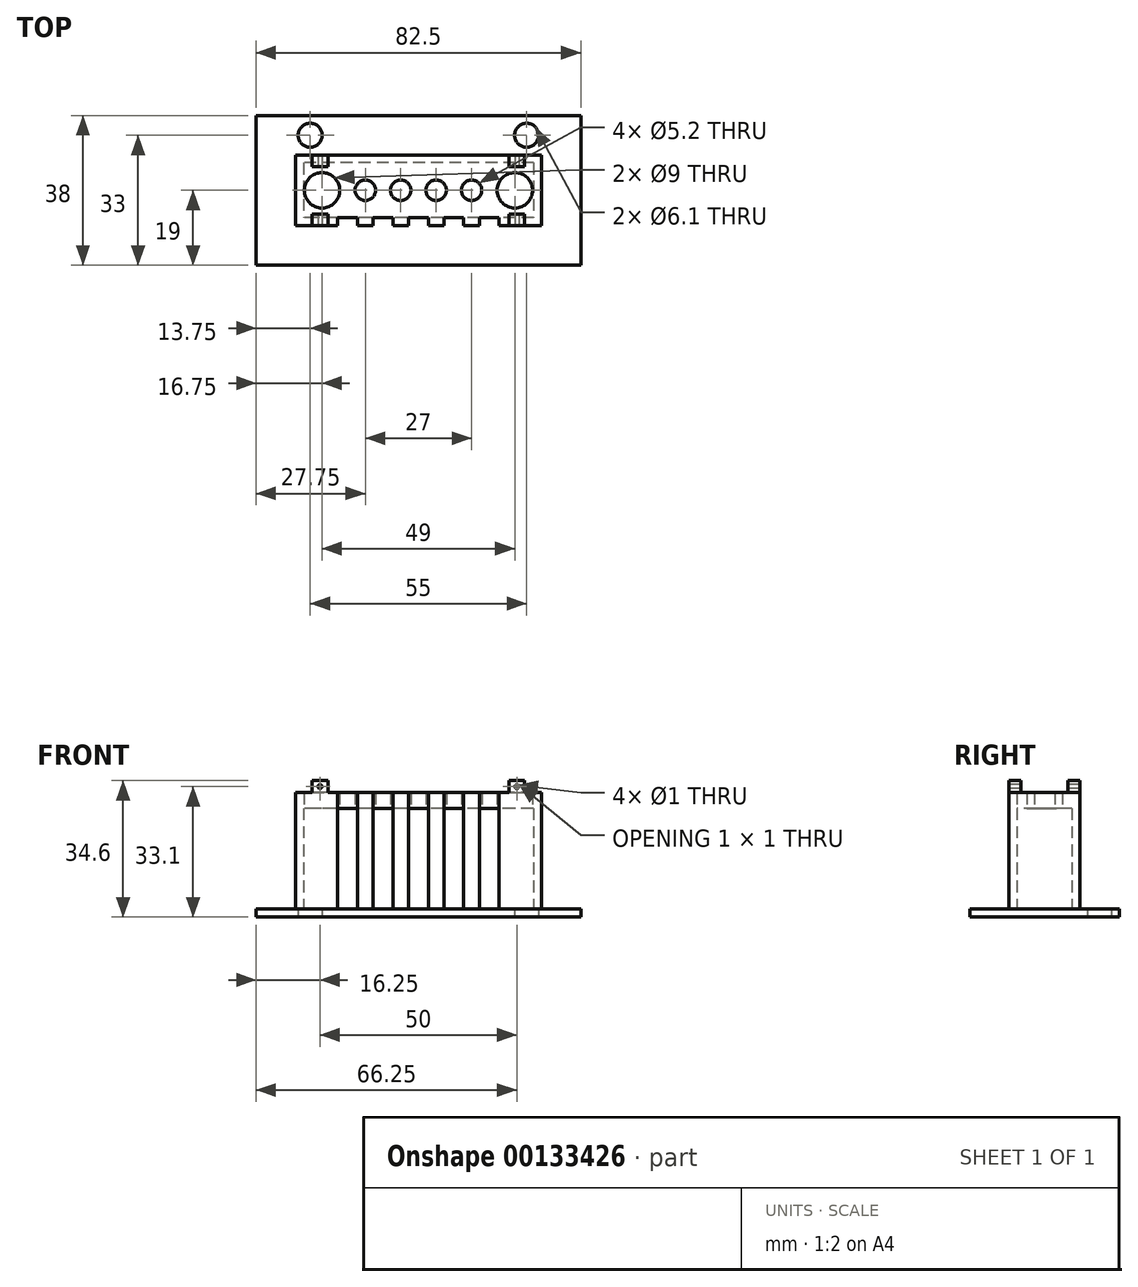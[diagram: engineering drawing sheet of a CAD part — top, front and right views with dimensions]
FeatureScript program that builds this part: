
annotation { "Feature Type Name" : "Feature", "Feature Type Description" : "" }
export const myFeature = defineFeature(function(context is Context, id is Id, definition is map)
    precondition{}
    {
        {
            var Q0;
            Q0=qCreatedBy(makeId("Top.planeOp"),FACE);
            var sketch = newSketch(context, id + "F0", { "sketchPlane" : qUnion([Q0])});
            skLineSegment(sketch, "E0.bottom", {"start": v(31.25, 9) * mm, "end": v(-31.25, 9) * mm});
            skLineSegment(sketch, "E0.top", {"start": v(31.25, -9) * mm, "end": v(-31.25, -9) * mm});
            skLineSegment(sketch, "E0.left", {"start": v(31.25, 9) * mm, "end": v(31.25, -9) * mm});
            skLineSegment(sketch, "E0.right", {"start": v(-31.25, 9) * mm, "end": v(-31.25, -9) * mm});
            skPoint(sketch, "E0.middle", {"position": v(0, 0) * mm});
            skLineSegment(sketch, "E1", {"start": v(-31.25, -9) * mm, "end": v(-31.25, 0) * mm});
            skLineSegment(sketch, "E2", {"start": v(-31.25, 0) * mm, "end": v(31.25, 0) * mm});
            skLineSegment(sketch, "E3", {"start": v(-13.5, 0) * mm, "end": v(-4.5, 0) * mm, "construction": true});
            skCircle(sketch, "E4", {"center": v(-4.5, 0) * mm, "radius": 2.6 * mm});
            skCircle(sketch, "E5.MirrorC", {"center": v(4.5, 0) * mm, "radius": 2.6 * mm});
            skLineSegment(sketch, "E6.0", {"start": v(29.25, -7) * mm, "end": v(-29.25, -7) * mm});
            skLineSegment(sketch, "E6.1", {"start": v(29.25, 7) * mm, "end": v(29.25, -7) * mm});
            skLineSegment(sketch, "E6.2", {"start": v(29.25, 7) * mm, "end": v(-29.25, 7) * mm});
            skLineSegment(sketch, "E6.3", {"start": v(-29.25, 7) * mm, "end": v(-29.25, -7) * mm});
            skCircle(sketch, "E7", {"center": v(-13.5, 0) * mm, "radius": 2.6 * mm});
            skLineSegment(sketch, "E8", {"start": v(4.5, 0) * mm, "end": v(4.5, 0) * mm});
            skCircle(sketch, "E9.MirrorC", {"center": v(13.5, 0) * mm, "radius": 2.6 * mm});
            skLineSegment(sketch, "E10.0", {"start": v(41.25, 19) * mm, "end": v(-41.25, 19) * mm});
            skLineSegment(sketch, "E10.1", {"start": v(41.25, 19) * mm, "end": v(41.25, -19) * mm});
            skLineSegment(sketch, "E10.2", {"start": v(41.25, -19) * mm, "end": v(-41.25, -19) * mm});
            skLineSegment(sketch, "E10.3", {"start": v(-41.25, 19) * mm, "end": v(-41.25, -19) * mm});
            skLineSegment(sketch, "E11", {"start": v(-41.25, 19) * mm, "end": v(-41.25, 14) * mm});
            skLineSegment(sketch, "E12", {"start": v(-41.25, 14) * mm, "end": v(-36.25, 14) * mm});
            skLineSegment(sketch, "E13", {"start": v(-13.5, 0) * mm, "end": v(-36.25, 0) * mm});
            skLineSegment(sketch, "E14", {"start": v(-36.25, 0) * mm, "end": v(-36.25, 14) * mm});
            skCircle(sketch, "E15.MirrorC", {"center": v(27.5, 14) * mm, "radius": 3.05 * mm});
            skCircle(sketch, "E16.MirrorC", {"center": v(-27.5, 14) * mm, "radius": 3.05 * mm});
            skLineSegment(sketch, "E17", {"start": v(0, 0) * mm, "end": v(24.5, 0) * mm});
            skCircle(sketch, "E18", {"center": v(24.5, 0) * mm, "radius": 4.5 * mm});
            skCircle(sketch, "E19.MirrorC", {"center": v(-24.5, 0) * mm, "radius": 4.5 * mm});
            skSolve(sketch);
        }
        {
            var Q0;
            {var subQ8=sQuery(id+"F0.wireOp",EDGE,"E0.top");Q0=makeQuery(id+"F0.imprint","IMPRINT",FACE,{"disambiguationData":[TD([[makeQuery(id+"F0.imprint","IMPRINT",EDGE,{"derivedFrom":subQ8}),-1.0]])]});}
            var Q1;
            {var subQ6=sQuery(id+"F0.wireOp",EDGE,"E0.bottom");Q1=makeQuery(id+"F0.imprint","IMPRINT",FACE,{"disambiguationData":[TD([[makeQuery(id+"F0.imprint","IMPRINT",EDGE,{"derivedFrom":subQ6}),1.0]])]});}
            extrude(context, id + "F1", {"entities" : qUnion([Q0, Q1]), "depth" : 31.6 * mm});
        }
        {
            var Q0;
            {var subQ8=sQuery(id+"F0.wireOp",EDGE,"E6.2");Q0=makeQuery(id+"F0.imprint","IMPRINT",FACE,{"disambiguationData":[TD([[makeQuery(id+"F0.imprint","IMPRINT",EDGE,{"derivedFrom":subQ8}),1.0]])]});}
            var Q1;
            {var subQ0=sQuery(id+"F0.wireOp",EDGE,"E6.0");Q1=makeQuery(id+"F0.imprint","IMPRINT",FACE,{"disambiguationData":[TD([[makeQuery(id+"F0.imprint","IMPRINT",EDGE,{"derivedFrom":subQ0}),-1.0]])]});}
            extrude(context, id + "F2", {"entities" : qUnion([Q0, Q1]), "operationType" : NewBodyOperationType.ADD, "depth" : 31.6 * mm, "hasSecondDirection" : true, "secondDirectionOppositeDirection" : false, "secondDirectionDepth" : 27.6 * mm});
        }
        {
            var Q0;
            {var subQ0=sQuery(id+"F0.wireOp",EDGE,"E0.bottom");Q0=makeQuery(id+"F0.imprint","IMPRINT",FACE,{"disambiguationData":[TD([[makeQuery(id+"F0.imprint","IMPRINT",EDGE,{"derivedFrom":subQ0}),-1.0]])]});}
            extrude(context, id + "F3", {"entities" : qUnion([Q0]), "operationType" : NewBodyOperationType.ADD, "depth" : 2 * mm});
        }
        {
            var Q0;
            Q0=makeQuery(id+"F1.opExtrude","SWEPT_FACE",FACE,{"disambiguationData":[OSD([sQuery(id+"F0.wireOp",EDGE,"E0.top")])]});
            var sketch = newSketch(context, id + "F4", { "sketchPlane" : qUnion([Q0])});
            skLineSegment(sketch, "E20", {"start": v(0, 2) * mm, "end": v(0, 31.6) * mm});
            skLineSegment(sketch, "E21.bottom", {"start": v(2.5, 31.6) * mm, "end": v(-2.5, 31.6) * mm});
            skLineSegment(sketch, "E21.top", {"start": v(2.5, 2) * mm, "end": v(-2.5, 2) * mm});
            skLineSegment(sketch, "E21.left", {"start": v(2.5, 31.6) * mm, "end": v(2.5, 2) * mm});
            skLineSegment(sketch, "E21.right", {"start": v(-2.5, 31.6) * mm, "end": v(-2.5, 2) * mm});
            skPoint(sketch, "E21.middle", {"position": v(0, 16.8) * mm});
            skLineSegment(sketch, "E22", {"start": v(0, 2) * mm, "end": v(-9, 2) * mm});
            skLineSegment(sketch, "E23", {"start": v(0, 2) * mm, "end": v(9, 2) * mm});
            skLineSegment(sketch, "E24", {"start": v(9, 2) * mm, "end": v(18, 2) * mm});
            skLineSegment(sketch, "E25", {"start": v(-9, 2) * mm, "end": v(-18, 2) * mm});
            skLineSegment(sketch, "E26", {"start": v(-18, 2) * mm, "end": v(-18, 31.6) * mm});
            skLineSegment(sketch, "E27", {"start": v(-9, 2) * mm, "end": v(-9, 31.6) * mm});
            skLineSegment(sketch, "E28", {"start": v(9, 2) * mm, "end": v(9, 31.6) * mm});
            skLineSegment(sketch, "E29", {"start": v(18, 2) * mm, "end": v(18, 31.6) * mm});
            skLineSegment(sketch, "E30.bottom", {"start": v(-15.5, 31.6) * mm, "end": v(-20.5, 31.6) * mm});
            skLineSegment(sketch, "E30.top", {"start": v(-15.5, 2) * mm, "end": v(-20.5, 2) * mm});
            skLineSegment(sketch, "E30.left", {"start": v(-15.5, 31.6) * mm, "end": v(-15.5, 2) * mm});
            skLineSegment(sketch, "E30.right", {"start": v(-20.5, 31.6) * mm, "end": v(-20.5, 2) * mm});
            skPoint(sketch, "E30.middle", {"position": v(-18, 16.8) * mm});
            skLineSegment(sketch, "E31.bottom", {"start": v(-6.5, 31.6) * mm, "end": v(-11.5, 31.6) * mm});
            skLineSegment(sketch, "E31.top", {"start": v(-6.5, 2) * mm, "end": v(-11.5, 2) * mm});
            skLineSegment(sketch, "E31.left", {"start": v(-6.5, 31.6) * mm, "end": v(-6.5, 2) * mm});
            skLineSegment(sketch, "E31.right", {"start": v(-11.5, 31.6) * mm, "end": v(-11.5, 2) * mm});
            skPoint(sketch, "E31.middle", {"position": v(-9, 16.8) * mm});
            skLineSegment(sketch, "E32.bottom", {"start": v(11.5, 31.6) * mm, "end": v(6.5, 31.6) * mm});
            skLineSegment(sketch, "E32.top", {"start": v(11.5, 2) * mm, "end": v(6.5, 2) * mm});
            skLineSegment(sketch, "E32.left", {"start": v(11.5, 31.6) * mm, "end": v(11.5, 2) * mm});
            skLineSegment(sketch, "E32.right", {"start": v(6.5, 31.6) * mm, "end": v(6.5, 2) * mm});
            skPoint(sketch, "E32.middle", {"position": v(9, 16.8) * mm});
            skLineSegment(sketch, "E33.bottom", {"start": v(20.5, 31.6) * mm, "end": v(15.5, 31.6) * mm});
            skLineSegment(sketch, "E33.top", {"start": v(20.5, 2) * mm, "end": v(15.5, 2) * mm});
            skLineSegment(sketch, "E33.left", {"start": v(20.5, 31.6) * mm, "end": v(20.5, 2) * mm});
            skLineSegment(sketch, "E33.right", {"start": v(15.5, 31.6) * mm, "end": v(15.5, 2) * mm});
            skPoint(sketch, "E33.middle", {"position": v(18, 16.8) * mm});
            skSolve(sketch);
        }
        {
            var Q0;
            {var subQ0=sQuery(id+"F4.wireOp",EDGE,"E20");Q0=makeQuery(id+"F4.imprint","IMPRINT",FACE,{"disambiguationData":[TD([[makeQuery(id+"F4.imprint","IMPRINT",EDGE,{"derivedFrom":subQ0}),1.0]])]});}
            var Q1;
            {var subQ0=sQuery(id+"F4.wireOp",EDGE,"E20");Q1=makeQuery(id+"F4.imprint","IMPRINT",FACE,{"disambiguationData":[TD([[makeQuery(id+"F4.imprint","IMPRINT",EDGE,{"derivedFrom":subQ0}),-1.0]])]});}
            var Q2;
            {var subQ0=sQuery(id+"F4.wireOp",EDGE,"E26");Q2=makeQuery(id+"F4.imprint","IMPRINT",FACE,{"disambiguationData":[TD([[makeQuery(id+"F4.imprint","IMPRINT",EDGE,{"derivedFrom":subQ0}),1.0]])]});}
            var Q3;
            {var subQ0=sQuery(id+"F4.wireOp",EDGE,"E26");Q3=makeQuery(id+"F4.imprint","IMPRINT",FACE,{"disambiguationData":[TD([[makeQuery(id+"F4.imprint","IMPRINT",EDGE,{"derivedFrom":subQ0}),-1.0]])]});}
            var Q4;
            {var subQ0=sQuery(id+"F4.wireOp",EDGE,"E27");Q4=makeQuery(id+"F4.imprint","IMPRINT",FACE,{"disambiguationData":[TD([[makeQuery(id+"F4.imprint","IMPRINT",EDGE,{"derivedFrom":subQ0}),1.0]])]});}
            var Q5;
            {var subQ0=sQuery(id+"F4.wireOp",EDGE,"E27");Q5=makeQuery(id+"F4.imprint","IMPRINT",FACE,{"disambiguationData":[TD([[makeQuery(id+"F4.imprint","IMPRINT",EDGE,{"derivedFrom":subQ0}),-1.0]])]});}
            var Q6;
            {var subQ0=sQuery(id+"F4.wireOp",EDGE,"E28");Q6=makeQuery(id+"F4.imprint","IMPRINT",FACE,{"disambiguationData":[TD([[makeQuery(id+"F4.imprint","IMPRINT",EDGE,{"derivedFrom":subQ0}),-1.0]])]});}
            var Q7;
            {var subQ0=sQuery(id+"F4.wireOp",EDGE,"E28");Q7=makeQuery(id+"F4.imprint","IMPRINT",FACE,{"disambiguationData":[TD([[makeQuery(id+"F4.imprint","IMPRINT",EDGE,{"derivedFrom":subQ0}),1.0]])]});}
            var Q8;
            {var subQ0=sQuery(id+"F4.wireOp",EDGE,"E29");Q8=makeQuery(id+"F4.imprint","IMPRINT",FACE,{"disambiguationData":[TD([[makeQuery(id+"F4.imprint","IMPRINT",EDGE,{"derivedFrom":subQ0}),1.0]])]});}
            var Q9;
            {var subQ0=sQuery(id+"F4.wireOp",EDGE,"E29");Q9=makeQuery(id+"F4.imprint","IMPRINT",FACE,{"disambiguationData":[TD([[makeQuery(id+"F4.imprint","IMPRINT",EDGE,{"derivedFrom":subQ0}),-1.0]])]});}
            extrude(context, id + "F5", {"entities" : qUnion([Q0, Q1, Q2, Q3, Q4, Q5, Q6, Q7, Q8, Q9]), "operationType" : NewBodyOperationType.REMOVE, "oppositeDirection" : true, "depth" : 2 * mm});
        }
        {
            var Q0;
            {var subQ0=sQuery(id+"F0.wireOp",EDGE,"E6.3");var subQ1=sQuery(id+"F0.wireOp",EDGE,"E6.2");var subQ2=sQuery(id+"F0.wireOp",EDGE,"E6.1");var subQ3=sQuery(id+"F0.wireOp",EDGE,"E6.0");Q0=makeQuery(id+"F2.boolean.opBoolean","MERGE",FACE,{"derivedFrom":[makeQuery(id+"F1.opExtrude","CAP_FACE",FACE,{"disambiguationData":[OSD([sQuery(id+"F0.wireOp",EDGE,"E0.bottom"),sQuery(id+"F0.wireOp",EDGE,"E0.top"),sQuery(id+"F0.wireOp",EDGE,"E0.left"),sQuery(id+"F0.wireOp",EDGE,"E0.right"),sQuery(id+"F0.wireOp",EDGE,"E1"),subQ3,subQ2,subQ1,subQ0])],"isStart":false}),makeQuery(id+"F2.opExtrude","CAP_FACE",FACE,{"disambiguationData":[OSD([sQuery(id+"F0.wireOp",EDGE,"E4"),sQuery(id+"F0.wireOp",EDGE,"E5.MirrorC"),subQ3,subQ2,subQ1,subQ0,sQuery(id+"F0.wireOp",EDGE,"E7"),sQuery(id+"F0.wireOp",EDGE,"E9.MirrorC"),sQuery(id+"F0.wireOp",EDGE,"E18"),sQuery(id+"F0.wireOp",EDGE,"E19.MirrorC")])],"isStart":false})]});}
            var sketch = newSketch(context, id + "F6", { "sketchPlane" : qUnion([Q0])});
            skLineSegment(sketch, "E34", {"start": v(-31.25, -9) * mm, "end": v(-29, -9) * mm});
            skLineSegment(sketch, "E35", {"start": v(-29, -9) * mm, "end": v(-25, -9) * mm});
            skLineSegment(sketch, "E36", {"start": v(-25, -9) * mm, "end": v(-27, -9) * mm});
            skLineSegment(sketch, "E37", {"start": v(-25, -9) * mm, "end": v(-23, -9) * mm});
            skLineSegment(sketch, "E38", {"start": v(-23, -9) * mm, "end": v(-23, -6) * mm});
            skLineSegment(sketch, "E39", {"start": v(-23, -6) * mm, "end": v(-25, -6) * mm});
            skLineSegment(sketch, "E40", {"start": v(-25, -6) * mm, "end": v(-27, -6) * mm});
            skLineSegment(sketch, "E41", {"start": v(-27, -6) * mm, "end": v(-27, -9) * mm});
            skLineSegment(sketch, "E42.MirrorCS", {"start": v(23, -9) * mm, "end": v(23, -6) * mm});
            skLineSegment(sketch, "E43.MirrorCS", {"start": v(23, -6) * mm, "end": v(25, -6) * mm});
            skLineSegment(sketch, "E44.MirrorCS", {"start": v(25, -6) * mm, "end": v(27, -6) * mm});
            skLineSegment(sketch, "E45.MirrorCS", {"start": v(27, -6) * mm, "end": v(27, -9) * mm});
            skLineSegment(sketch, "E46.MirrorCS", {"start": v(25, -9) * mm, "end": v(27, -9) * mm});
            skLineSegment(sketch, "E47.MirrorCS", {"start": v(25, -9) * mm, "end": v(23, -9) * mm});
            skLineSegment(sketch, "E48.MirrorCS", {"start": v(-23, 9) * mm, "end": v(-23, 6) * mm});
            skLineSegment(sketch, "E49.MirrorCS", {"start": v(-23, 6) * mm, "end": v(-25, 6) * mm});
            skLineSegment(sketch, "E50.MirrorCS", {"start": v(-25, 6) * mm, "end": v(-27, 6) * mm});
            skLineSegment(sketch, "E51.MirrorCS", {"start": v(-27, 6) * mm, "end": v(-27, 9) * mm});
            skLineSegment(sketch, "E52.MirrorCS", {"start": v(-25, 9) * mm, "end": v(-27, 9) * mm});
            skLineSegment(sketch, "E53.MirrorCS", {"start": v(-25, 9) * mm, "end": v(-23, 9) * mm});
            skLineSegment(sketch, "E54.MirrorCS", {"start": v(27, 6) * mm, "end": v(27, 9) * mm});
            skLineSegment(sketch, "E55.MirrorCS", {"start": v(25, 6) * mm, "end": v(27, 6) * mm});
            skLineSegment(sketch, "E56.MirrorCS", {"start": v(23, 6) * mm, "end": v(25, 6) * mm});
            skLineSegment(sketch, "E57.MirrorCS", {"start": v(23, 9) * mm, "end": v(23, 6) * mm});
            skLineSegment(sketch, "E58.MirrorCS", {"start": v(25, 9) * mm, "end": v(23, 9) * mm});
            skLineSegment(sketch, "E59.MirrorCS", {"start": v(25, 9) * mm, "end": v(27, 9) * mm});
            skSolve(sketch);
        }
        {
            var Q0;
            Q0 = qSketchRegion(id + "F6", true);
            extrude(context, id + "F7", {"entities" : qUnion([Q0]), "operationType" : NewBodyOperationType.ADD, "depth" : 3 * mm});
        }
        {
            var Q0;
            {var subQ7=sQuery(id+"F0.wireOp",EDGE,"E0.top");Q0=makeQuery(id+"F7.boolean.opBoolean","MERGE",FACE,{"derivedFrom":[makeQuery(id+"F5.boolean.opBoolean","SPLIT",FACE,{"disambiguationData":[TD([makeQuery(id+"F5.opExtrude","SWEPT_FACE",FACE,{"disambiguationData":[OSD([sQuery(id+"F4.wireOp",EDGE,"E30.right")])]})])],"derivedFrom":makeQuery(id+"F1.opExtrude","SWEPT_FACE",FACE,{"disambiguationData":[OSD([subQ7])]})}),makeQuery(id+"F7.opExtrude","SWEPT_FACE",FACE,{"disambiguationData":[OSD([sQuery(id+"F6.wireOp",EDGE,"E36"),sQuery(id+"F6.wireOp",EDGE,"E37")])]})]});}
            var sketch = newSketch(context, id + "F8", { "sketchPlane" : qUnion([Q0])});
            skLineSegment(sketch, "E60", {"start": v(-27, 34.6) * mm, "end": v(-25, 34.6) * mm});
            skLineSegment(sketch, "E61", {"start": v(-25, 34.6) * mm, "end": v(-25, 33.1) * mm});
            skCircle(sketch, "E62", {"center": v(-25, 33.1) * mm, "radius": 0.5 * mm});
            skCircle(sketch, "E63.MirrorC", {"center": v(25, 33.1) * mm, "radius": 0.5 * mm});
            skSolve(sketch);
        }
        {
            var Q0;
            Q0 = qSketchRegion(id + "F8", true);
            extrude(context, id + "F9", {"entities" : qUnion([Q0]), "operationType" : NewBodyOperationType.REMOVE, "oppositeDirection" : true, "depth" : 25 * mm});
        }
    });
